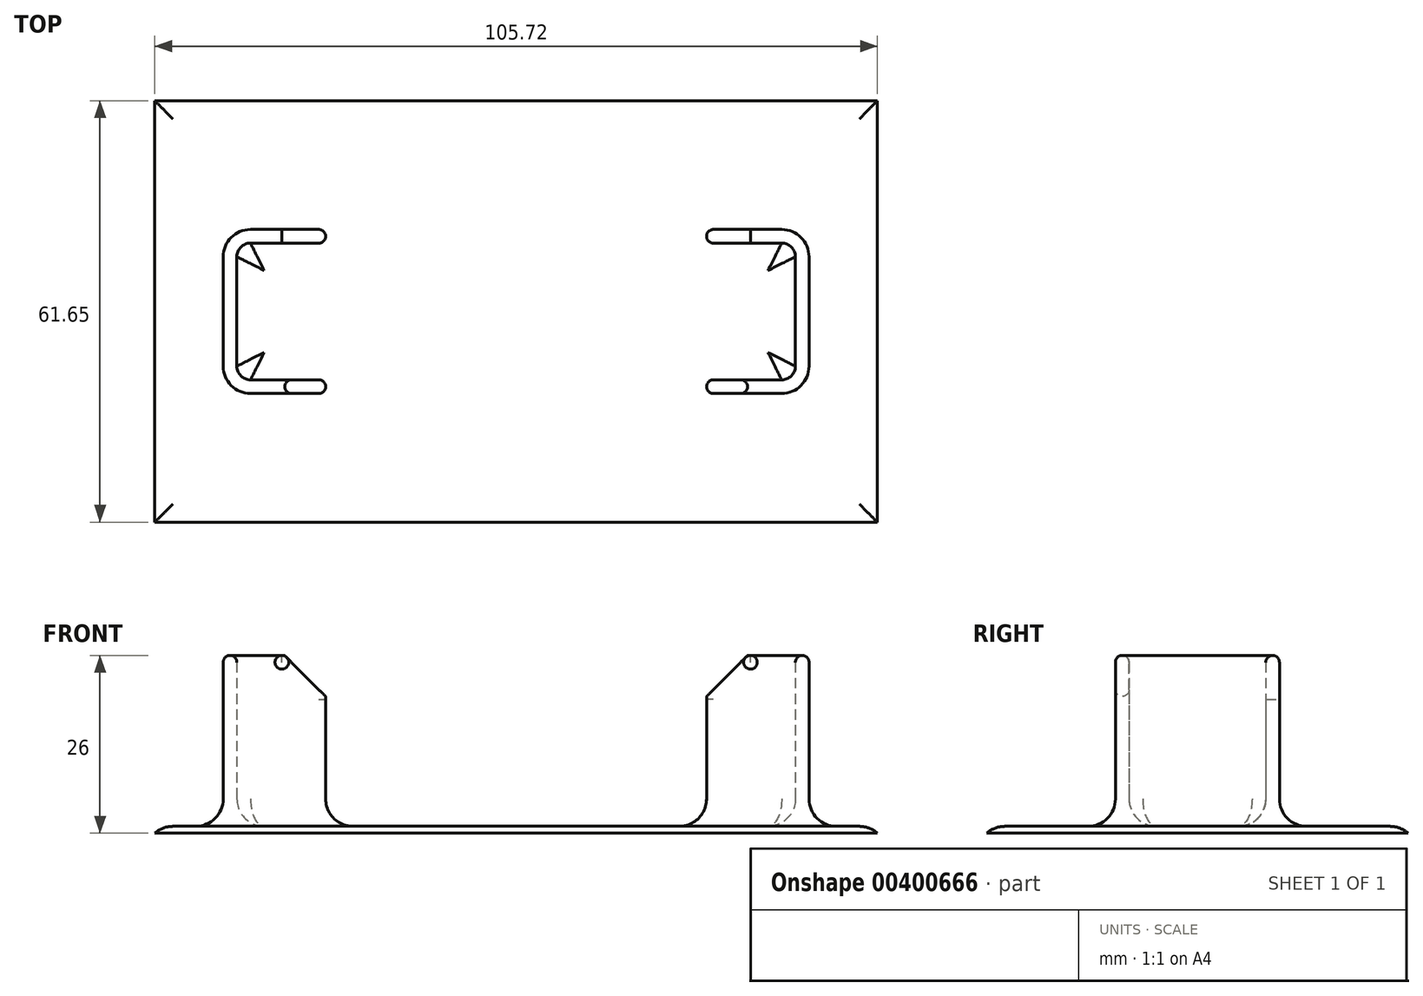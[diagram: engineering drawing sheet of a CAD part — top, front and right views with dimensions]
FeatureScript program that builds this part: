
annotation { "Feature Type Name" : "Feature", "Feature Type Description" : "" }
export const myFeature = defineFeature(function(context is Context, id is Id, definition is map)
    precondition{}
    {
        {
            var Q0;
            Q0=qCreatedBy(makeId("Top.planeOp"),FACE);
            var sketch = newSketch(context, id + "F0", { "sketchPlane" : qUnion([Q0])});
            skLineSegment(sketch, "E0.bottom", {"start": v(-52.86, 31.07) * mm, "end": v(40.82, 31.07) * mm});
            skLineSegment(sketch, "E0.top", {"start": v(-52.86, -30.58) * mm, "end": v(40.82, -30.58) * mm});
            skLineSegment(sketch, "E0.left", {"start": v(-52.86, 31.07) * mm, "end": v(-52.86, -30.58) * mm});
            skLineSegment(sketch, "E0.right", {"start": v(40.82, 31.07) * mm, "end": v(40.82, -30.58) * mm});
            skSolve(sketch);
        }
        {
            var Q0;
            Q0 = qSketchRegion(id + "F0", true);
            extrude(context, id + "F1", {"entities" : qUnion([Q0]), "oppositeDirection" : true, "depth" : 1 * mm});
        }
        {
            var Q0;
            Q0=makeQuery(id+"F1.opExtrude","CAP_FACE",FACE,{"disambiguationData":[OSD([sQuery(id+"F0.wireOp",EDGE,"E0.bottom"),sQuery(id+"F0.wireOp",EDGE,"E0.top"),sQuery(id+"F0.wireOp",EDGE,"E0.left"),sQuery(id+"F0.wireOp",EDGE,"E0.right")])],"isStart":true});
            var sketch = newSketch(context, id + "F2", { "sketchPlane" : qUnion([Q0])});
            skLineSegment(sketch, "E1", {"start": v(-40.86, 10.24) * mm, "end": v(-40.86, -9.76) * mm});
            skLineSegment(sketch, "E2", {"start": v(-40.86, -9.76) * mm, "end": v(-27.86, -9.76) * mm});
            skLineSegment(sketch, "E3", {"start": v(-27.86, -11.76) * mm, "end": v(-27.86, -9.76) * mm});
            skLineSegment(sketch, "E4", {"start": v(-27.86, -11.76) * mm, "end": v(-42.86, -11.76) * mm});
            skLineSegment(sketch, "E5", {"start": v(-42.86, -11.76) * mm, "end": v(-42.86, 12.24) * mm});
            skLineSegment(sketch, "E6", {"start": v(-42.86, 12.24) * mm, "end": v(-27.86, 12.24) * mm});
            skLineSegment(sketch, "E7", {"start": v(-27.86, 10.24) * mm, "end": v(-27.86, 12.24) * mm});
            skLineSegment(sketch, "E8", {"start": v(-27.86, 10.24) * mm, "end": v(-40.86, 10.24) * mm});
            skLineSegment(sketch, "E9", {"start": v(-52.86, 0.24) * mm, "end": v(40.82, 0.24) * mm, "construction": true});
            skLineSegment(sketch, "E10", {"start": v(-40.86, -9.76) * mm, "end": v(-42.86, -9.76) * mm, "construction": true});
            skLineSegment(sketch, "E11", {"start": v(-6.02, -30.58) * mm, "end": v(-6.02, 31.07) * mm, "construction": true});
            skSolve(sketch);
        }
        {
            var Q0;
            Q0 = qSketchRegion(id + "F2", true);
            extrude(context, id + "F3", {"entities" : qUnion([Q0]), "operationType" : NewBodyOperationType.ADD, "depth" : 25 * mm});
        }
        {
            var Q0;
            Q0=makeQuery(id+"F3.opExtrude","SWEPT_EDGE",EDGE,{"disambiguationData":[OSD([sQuery(id+"F2.wireOp",EDGE,"E1"),sQuery(id+"F2.wireOp",EDGE,"E8")])]});
            var Q1;
            Q1=makeQuery(id+"F3.opExtrude","SWEPT_EDGE",EDGE,{"disambiguationData":[OSD([sQuery(id+"F2.wireOp",EDGE,"E1"),sQuery(id+"F2.wireOp",EDGE,"E2")])]});
            fillet(context, id + "F4", {"entities" : qUnion([Q0, Q1]), "radius" : 2 * mm, "tangentPropagation" : true, "allowEdgeOverflow" : false});
        }
        {
            var Q0;
            Q0=makeQuery(id+"F3.opExtrude","SWEPT_EDGE",EDGE,{"disambiguationData":[OSD([sQuery(id+"F2.wireOp",EDGE,"E5"),sQuery(id+"F2.wireOp",EDGE,"E6")])]});
            var Q1;
            Q1=makeQuery(id+"F3.opExtrude","SWEPT_EDGE",EDGE,{"disambiguationData":[OSD([sQuery(id+"F2.wireOp",EDGE,"E4"),sQuery(id+"F2.wireOp",EDGE,"E5")])]});
            fillet(context, id + "F5", {"entities" : qUnion([Q0, Q1]), "radius" : 4 * mm, "tangentPropagation" : true, "allowEdgeOverflow" : false});
        }
        {
            var Q0;
            Q0=makeQuery(id+"F3.opExtrude","SWEPT_EDGE",EDGE,{"disambiguationData":[OSD([sQuery(id+"F2.wireOp",EDGE,"E3"),sQuery(id+"F2.wireOp",EDGE,"E4")])]});
            var Q1;
            Q1=makeQuery(id+"F3.opExtrude","SWEPT_EDGE",EDGE,{"disambiguationData":[OSD([sQuery(id+"F2.wireOp",EDGE,"E2"),sQuery(id+"F2.wireOp",EDGE,"E3")])]});
            var Q2;
            Q2=makeQuery(id+"F3.opExtrude","SWEPT_EDGE",EDGE,{"disambiguationData":[OSD([sQuery(id+"F2.wireOp",EDGE,"E7"),sQuery(id+"F2.wireOp",EDGE,"E8")])]});
            var Q3;
            Q3=makeQuery(id+"F3.opExtrude","SWEPT_EDGE",EDGE,{"disambiguationData":[OSD([sQuery(id+"F2.wireOp",EDGE,"E6"),sQuery(id+"F2.wireOp",EDGE,"E7")])]});
            fillet(context, id + "F6", {"entities" : qUnion([Q0, Q1, Q2, Q3]), "radius" : 1 * mm, "tangentPropagation" : true, "allowEdgeOverflow" : false});
        }
        {
            var Q0;
            Q0=makeQuery(id+"F3.opExtrude","CAP_EDGE",EDGE,{"disambiguationData":[OSD([sQuery(id+"F2.wireOp",EDGE,"E1")])],"isStart":false});
            fillet(context, id + "F7", {"entities" : qUnion([Q0]), "radius" : 1 * mm, "tangentPropagation" : true, "allowEdgeOverflow" : false});
        }
        {
            var Q0;
            Q0=makeQuery(id+"F3.opExtrude","SWEPT_FACE",FACE,{"disambiguationData":[OSD([sQuery(id+"F2.wireOp",EDGE,"E4")])]});
            var sketch = newSketch(context, id + "F8", { "sketchPlane" : qUnion([Q0])});
            skLineSegment(sketch, "E12.0", {"start": v(-38.86, 24) * mm, "end": v(-38.86, 0) * mm, "construction": true});
            skLineSegment(sketch, "E13", {"start": v(-27.86, 24) * mm, "end": v(-27.86, 0) * mm, "construction": true});
            skPoint(sketch, "E14.0", {"position": v(-33.86, 0) * mm});
            skLineSegment(sketch, "E15.0", {"start": v(-28.86, 0) * mm, "end": v(-38.86, 0) * mm, "construction": true});
            skLineSegment(sketch, "E16", {"start": v(-33.86, 25) * mm, "end": v(-27.86, 19) * mm});
            skLineSegment(sketch, "E17", {"start": v(-38.86, 24) * mm, "end": v(-38.86, 25) * mm, "construction": true});
            skLineSegment(sketch, "E18", {"start": v(-38.86, 25) * mm, "end": v(-33.86, 25) * mm, "construction": true});
            skLineSegment(sketch, "E19", {"start": v(-33.86, 25) * mm, "end": v(-27.86, 25) * mm});
            skLineSegment(sketch, "E20", {"start": v(-27.86, 25) * mm, "end": v(-27.86, 19) * mm});
            skSolve(sketch);
        }
        {
            var Q0;
            Q0 = qSketchRegion(id + "F8", true);
            extrude(context, id + "F9", {"entities" : qUnion([Q0]), "operationType" : NewBodyOperationType.REMOVE, "oppositeDirection" : true, "depth" : 25 * mm});
        }
        {
            var Q0;
            Q0=makeQuery(id+"F9.boolean.opBoolean","COPY",EDGE,{"derivedFrom":makeQuery(id+"F9.opExtrude","CAP_EDGE",EDGE,{"disambiguationData":[OSD([sQuery(id+"F8.wireOp",EDGE,"E16")])],"isStart":true})});
            var Q1;
            Q1=makeQuery(id+"F9.boolean.opBoolean","INTERSECT",EDGE,{"derivedFrom":[makeQuery(id+"F3.opExtrude","SWEPT_FACE",FACE,{"disambiguationData":[OSD([sQuery(id+"F2.wireOp",EDGE,"E8")])]}),makeQuery(id+"F9.opExtrude","SWEPT_FACE",FACE,{"disambiguationData":[OSD([sQuery(id+"F8.wireOp",EDGE,"E16")])]})]});
            fillet(context, id + "F10", {"entities" : qUnion([Q0, Q1]), "radius" : 1 * mm, "tangentPropagation" : true, "allowEdgeOverflow" : false});
        }
        {
            var Q0;
            {var subQ0=makeQuery(id+"F1.opExtrude","CAP_FACE",FACE,{"disambiguationData":[OSD([sQuery(id+"F0.wireOp",EDGE,"E0.bottom"),sQuery(id+"F0.wireOp",EDGE,"E0.top"),sQuery(id+"F0.wireOp",EDGE,"E0.left"),sQuery(id+"F0.wireOp",EDGE,"E0.right")])],"isStart":true});Q0=makeQuery(id+"F12.boolean.opBoolean","MERGE",FACE,{"derivedFrom":[subQ0,makeQuery(id+"F12.opPattern","COPY",FACE,{"derivedFrom":subQ0,"instanceName":"1"})]});}
            fillet(context, id + "F11", {"entities" : qUnion([Q0]), "radius" : 4 * mm, "tangentPropagation" : true, "allowEdgeOverflow" : false});
        }
        {
            var Q0;
            Q0=makeQuery(id+"F1.opExtrude","SWEPT_BODY",BODY,{"disambiguationData":[OSD([sQuery(id+"F0.wireOp",EDGE,"E0.bottom"),sQuery(id+"F0.wireOp",EDGE,"E0.top"),sQuery(id+"F0.wireOp",EDGE,"E0.left"),sQuery(id+"F0.wireOp",EDGE,"E0.right")])]});
            var Q1;
            Q1=qCreatedBy(makeId("Right.planeOp"),FACE);
            mirror(context, id + "F12", {"operationType" : NewBodyOperationType.ADD, "entities" : qUnion([Q0]), "mirrorPlane" : qUnion([Q1])});
        }
    });
